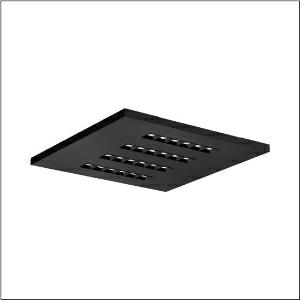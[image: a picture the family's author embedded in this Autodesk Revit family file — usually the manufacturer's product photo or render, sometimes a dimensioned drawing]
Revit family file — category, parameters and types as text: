
# Revit family: silica_21_square_51mx6kdu34b
name_source: partatom
category: Lighting Fixtures
units: mm (PartAtom-declared; Revit-internal decimal feet)

## family parameters
Cut with Voids When Loaded = No
Host = Face
Light Source = No
Part Type = Normal
Room Calculation Point = No
Round Connector Dimension = Use Diameter
Shared = No

## types (1)
- --- (1 x LED, 4600 lm, 31.9 W, 3000K)
    Apparent Load = 32 VA
    CIE Flux Codes = 86 100 100 100 100
    Color Rendering = 80
    Color Temperature = 3000K
    Default Elevation = 1800 mm
    Description = Silica 21 Square, office luminaire, primary light control with lens, of PMMA, primary anti-glare with reflector, of PC, black, CAT 2 (L<= 3000cd/m²), light emission: direct distribution, primary light characteristic: symmetric, installation type: lay-in mounting, LED, rated luminous flux: 4.600lm, luminous efficacy: 144lm/W, light colour: 830, colour temperature: 3000K, control gear: DALI 2, with terminal, 5-pole, mains connection: 220..240V, AC, 50/60Hz, rated input power: 31.9W, luminaire housing, of aluminium, matt jet black (RAL 9005), module: M625, length: 622mm, width: 622mm, height: 33mm, protection rating (complete): IP20, insulation class (complete): insulation class I (protective earthing), certification: CE, ENEC, VDE, permissible operating ambient temperature: -20..+40°C, standard: EN 50419, packaging unit: 1 piece
    Height = 0 mm  [stored 0 ft]
    Lamp = 1 x LED
    Lamp Light Flux = 4600 lm
    Lamp Power = 31.9 W
    Lamp count = 1
    Length = 622 mm
    Luminous efficacy = 144 lm/W
    Manufacturer = Siteco
    ModVariant = No
    Model = 51MX6KDU34B
    Mounting Place = Ceiling
    Mounting Type = Recessed
    Number of Poles = 1
    OnlyDefault = Yes
    Power Factor = 1
    Product Name = Silica 21 Square
    Product group = office luminaire | ceiling recessed
    ProductGroupID = 400
    Protection Class = Protection class I
    Protection Degree = IP 20
    RLX_Detail_Level = 1
    RLX_Emergency_Light_Flux = 0 lm
    RLX_Emergency_Type = 0
    RLX_Emergency_Type_DB = No
    RlxData = <blob elided: 24961 chars, md5=44a4c703>
    Socket = socket
    Standby Power = 0 W
    System Light Flux = 4600 lm
    System Power = 32 W
    Type Comments = factory setting: luminous flux: 100 % | dim-lin: 254 | 430 mA
    Type Image = l_1275204.jpg
    URL = http://relux.com
    VarID = @adj_090509
    Voltage = 0 V
    Weight = 0.00 kg
    Width = 622 mm

note: [stored X ft] marks values corroborated as IEEE doubles in the binary element streams (Revit-internal decimal feet)

## geometry (parser evidence)
native form markers: Blend x4, Sweep x11
no freeform markers — native parametric forms only
